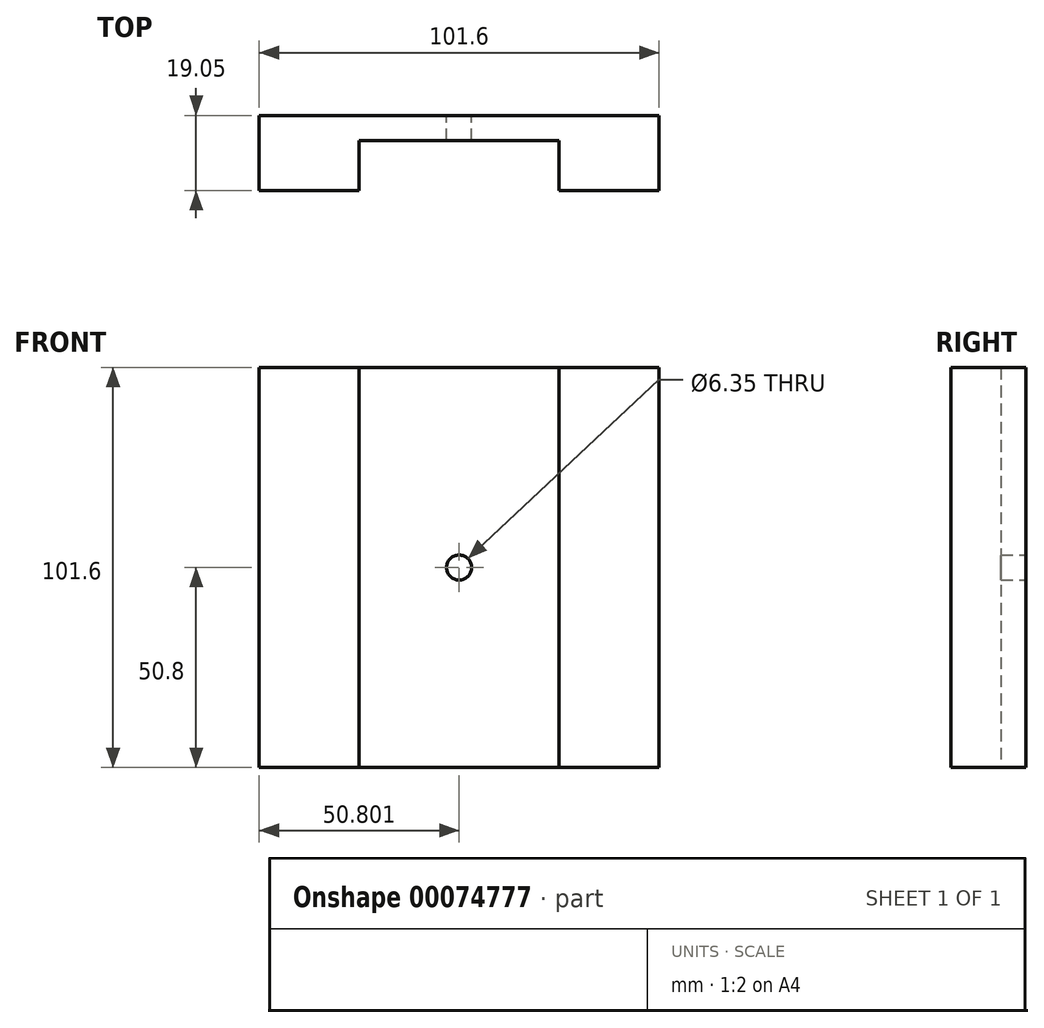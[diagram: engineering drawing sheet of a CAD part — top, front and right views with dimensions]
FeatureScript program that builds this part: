
annotation { "Feature Type Name" : "Feature", "Feature Type Description" : "" }
export const myFeature = defineFeature(function(context is Context, id is Id, definition is map)
    precondition{}
    {
        {
            var Q0;
            Q0=qCreatedBy(makeId("Top.planeOp"),FACE);
            var sketch = newSketch(context, id + "F0", { "sketchPlane" : qUnion([Q0])});
            skLineSegment(sketch, "E0", {"start": v(-8.8, -12.9) * mm, "end": v(-8.8, -25.6) * mm});
            skLineSegment(sketch, "E1", {"start": v(-8.8, -25.6) * mm, "end": v(42, -25.6) * mm});
            skLineSegment(sketch, "E2", {"start": v(42, -25.6) * mm, "end": v(42, -12.9) * mm});
            skLineSegment(sketch, "E3", {"start": v(42, -12.9) * mm, "end": v(-8.8, -12.9) * mm});
            skLineSegment(sketch, "E4", {"start": v(-34.2, -6.55) * mm, "end": v(67.4, -6.55) * mm});
            skLineSegment(sketch, "E5", {"start": v(67.4, -6.55) * mm, "end": v(67.4, -31.95) * mm});
            skLineSegment(sketch, "E6", {"start": v(67.4, -31.95) * mm, "end": v(-34.2, -31.95) * mm});
            skLineSegment(sketch, "E7", {"start": v(-34.2, -31.95) * mm, "end": v(-34.2, -6.55) * mm});
            skSolve(sketch);
        }
        {
            var Q0;
            Q0=makeQuery(id+"F0.imprint","IMPRINT",FACE,{"disambiguationData":[TD([[makeQuery(id+"F0.imprint","IMPRINT",EDGE,{"derivedFrom":sQuery(id+"F0.wireOp",EDGE,"E0")}),-1.0]])]});
            extrude(context, id + "F1", {"entities" : qUnion([Q0]), "depth" : 101.6 * mm});
        }
        {
            var Q0;
            Q0=makeQuery(id+"F1.opExtrude","CAP_FACE",FACE,{"disambiguationData":[OSD([sQuery(id+"F0.wireOp",EDGE,"E0"),sQuery(id+"F0.wireOp",EDGE,"E1"),sQuery(id+"F0.wireOp",EDGE,"E2"),sQuery(id+"F0.wireOp",EDGE,"E3"),sQuery(id+"F0.wireOp",EDGE,"E4"),sQuery(id+"F0.wireOp",EDGE,"E5"),sQuery(id+"F0.wireOp",EDGE,"E6"),sQuery(id+"F0.wireOp",EDGE,"E7")])],"isStart":false});
            var sketch = newSketch(context, id + "F2", { "sketchPlane" : qUnion([Q0])});
            skLineSegment(sketch, "E8", {"start": v(-8.8, -25.6) * mm, "end": v(-34.2, -25.6) * mm});
            skLineSegment(sketch, "E9", {"start": v(-34.2, -25.6) * mm, "end": v(-34.2, -31.95) * mm});
            skLineSegment(sketch, "E10", {"start": v(-34.2, -31.95) * mm, "end": v(67.4, -31.95) * mm});
            skLineSegment(sketch, "E11", {"start": v(67.4, -31.95) * mm, "end": v(67.4, -25.6) * mm});
            skLineSegment(sketch, "E12", {"start": v(67.4, -25.6) * mm, "end": v(42, -25.6) * mm});
            skLineSegment(sketch, "E13", {"start": v(42, -25.6) * mm, "end": v(-8.8, -25.6) * mm});
            skSolve(sketch);
        }
        {
            var Q0;
            Q0=makeQuery(id+"F2.imprint","IMPRINT",FACE,{"disambiguationData":[TD([[makeQuery(id+"F2.imprint","IMPRINT",EDGE,{"derivedFrom":sQuery(id+"F2.wireOp",EDGE,"E8")}),1.0]])]});
            extrude(context, id + "F3", {"entities" : qUnion([Q0]), "operationType" : NewBodyOperationType.REMOVE, "endBound" : BoundingType.THROUGH_ALL, "oppositeDirection" : true, "depth" : 25.4 * mm});
        }
        {
            var Q0;
            Q0=makeQuery(id+"F1.opExtrude","SWEPT_FACE",FACE,{"disambiguationData":[OSD([sQuery(id+"F0.wireOp",EDGE,"E4")])]});
            var sketch = newSketch(context, id + "F4", { "sketchPlane" : qUnion([Q0])});
            skPoint(sketch, "E14", {"position": v(-16.6, 50.8) * mm});
            skPoint(sketch, "E14.positionSnap0", {"position": v(-67.4, 50.8) * mm});
            skPoint(sketch, "E14.positionSnap1", {"position": v(-16.6, 101.6) * mm});
            skSolve(sketch);
        }
        {
            var Q0;
            Q0=sQuery(id+"F4.wireOp",VERTEX,"E14");
            var Q1;
            Q1=makeQuery(id+"F1.opExtrude","SWEPT_BODY",BODY,{"disambiguationData":[OSD([sQuery(id+"F0.wireOp",EDGE,"E0"),sQuery(id+"F0.wireOp",EDGE,"E1"),sQuery(id+"F0.wireOp",EDGE,"E2"),sQuery(id+"F0.wireOp",EDGE,"E3"),sQuery(id+"F0.wireOp",EDGE,"E4"),sQuery(id+"F0.wireOp",EDGE,"E5"),sQuery(id+"F0.wireOp",EDGE,"E6"),sQuery(id+"F0.wireOp",EDGE,"E7")])]});
            hole(context, id + "F5", {"style" : HoleStyle.SIMPLE, "holeDiameter" : 6.35 * mm, "endStyle" : HoleEndStyle.THROUGH, "locations" : qUnion([Q0]), "scope" : qUnion([Q1])});
        }
    });
